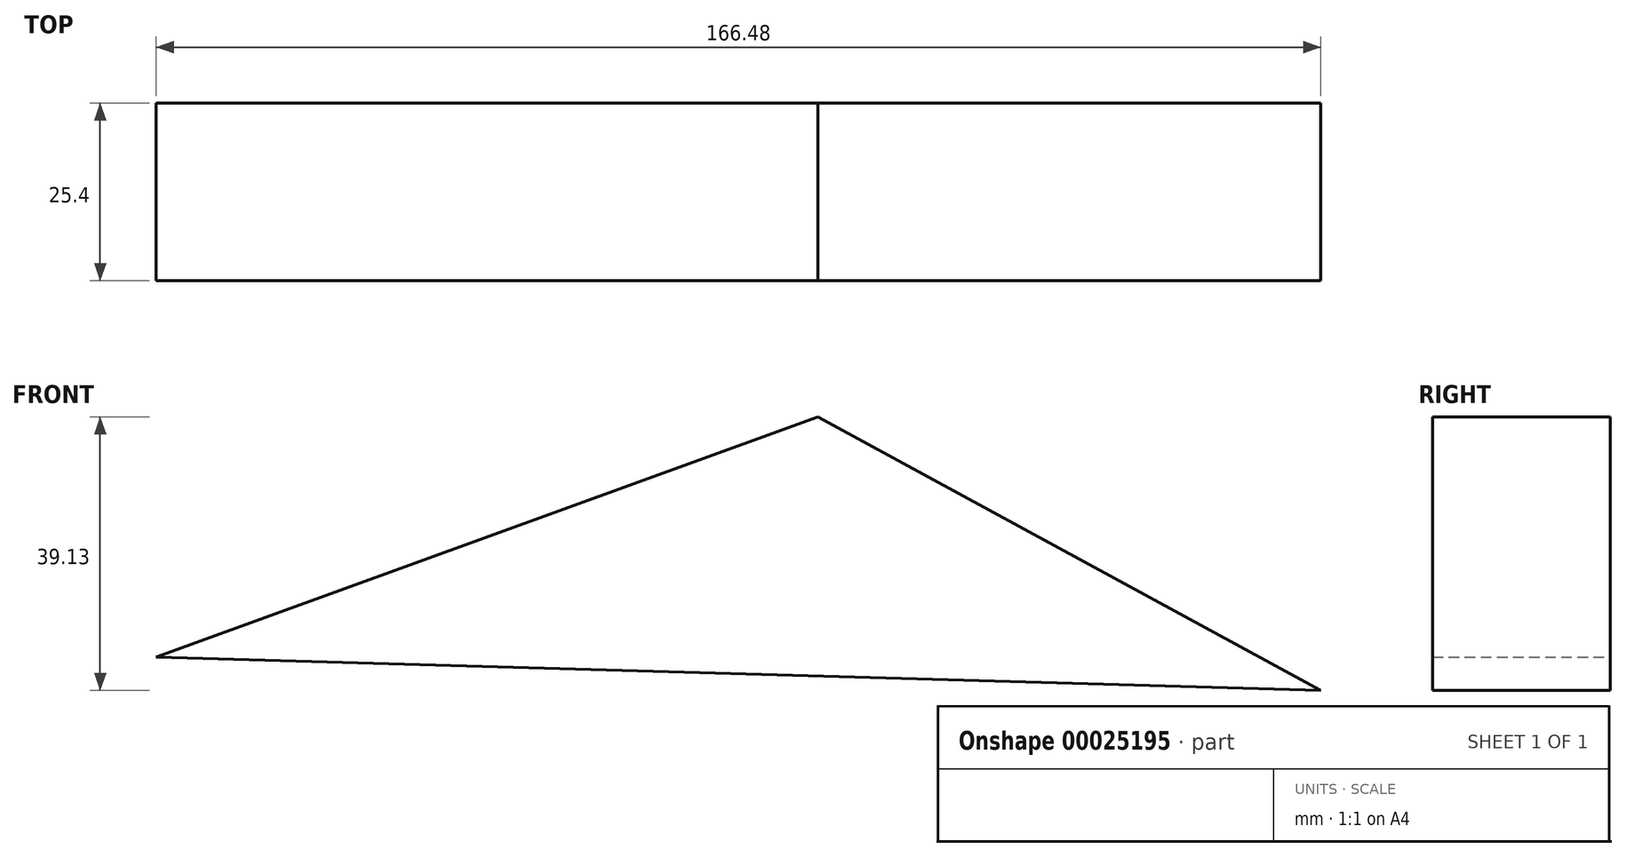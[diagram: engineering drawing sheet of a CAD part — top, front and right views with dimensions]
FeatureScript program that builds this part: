
annotation { "Feature Type Name" : "Feature", "Feature Type Description" : "" }
export const myFeature = defineFeature(function(context is Context, id is Id, definition is map)
    precondition{}
    {
        {
            var Q0;
            Q0=qCreatedBy(makeId("Front.planeOp"),FACE);
            var sketch = newSketch(context, id + "F0", { "sketchPlane" : qUnion([Q0])});
            skLineSegment(sketch, "E0", {"start": v(-94.6, -34.37) * mm, "end": v(0, 0) * mm});
            skLineSegment(sketch, "E1", {"start": v(0, 0) * mm, "end": v(71.89, -39.13) * mm});
            skLineSegment(sketch, "E2", {"start": v(71.89, -39.13) * mm, "end": v(-94.6, -34.37) * mm});
            skSolve(sketch);
        }
        {
            var Q0;
            Q0 = qSketchRegion(id + "F0", true);
            extrude(context, id + "F1", {"entities" : qUnion([Q0]), "depth" : 25.4 * mm});
        }
    });
